# Revit family: Sanitary_Taps-Mixers_AXOR_47440XXX-AXOR-MyEdition-Single-lever-bat__865554
name_source: partatom
category: Plumbing Fixtures
revit_build: Autodesk Revit 2018 (Build: 20170223_1515(x64)
units: mm (PartAtom-declared; Revit-internal decimal feet)

## family parameters
Always vertical = No
Cut with Voids When Loaded = No
OmniClass Number = 23.31.11.00
OmniClass Title = Faucets
Part Type = Normal
Room Calculation Point = No
Round Connector Dimension = Use Diameter
Shared = No
Work Plane-Based = Yes

## types (1)
- Matte Black/Black Glass
    Default Elevation = 1219 mm
    Description = AXOR MyEdition Single lever bath mixer floor-standing
    Edition number = 0
    Manufacturer = AXOR
    Material = AXOR - Metal - 670 Matte Black
    Material 1 = AXOR - Glass - Black Glass
    Model = 47440XXX
    Product Guid = cec036ba-affa-4227-8ee4-4c6e93638b28
    Product Page URL = https://www.axor-design.com
    Product data url = https://bimobject.com
    URL = https://www.axor-design.com
    Version = 1

## geometry (parser evidence)
native form markers: Sweep x2
no freeform markers — native parametric forms only
